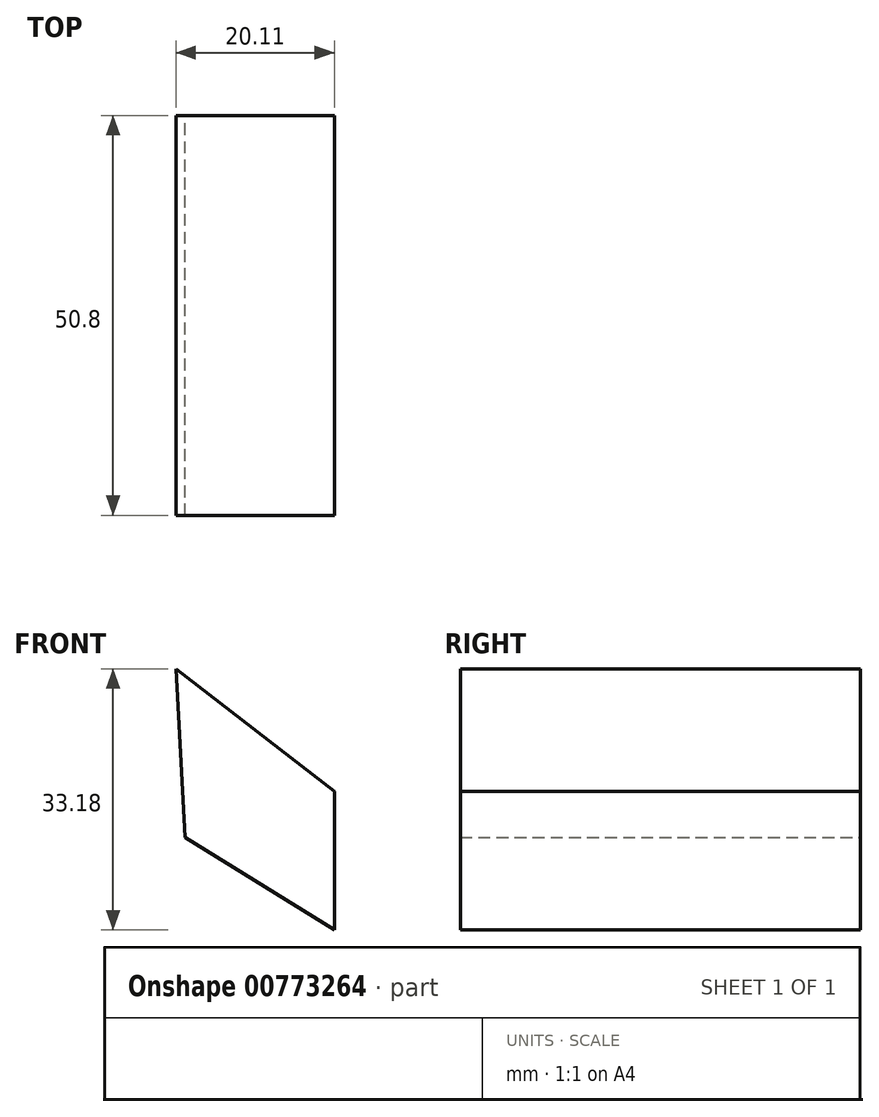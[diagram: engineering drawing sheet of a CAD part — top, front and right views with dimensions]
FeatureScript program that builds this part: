
annotation { "Feature Type Name" : "Feature", "Feature Type Description" : "" }
export const myFeature = defineFeature(function(context is Context, id is Id, definition is map)
    precondition{}
    {
        {
            var Q0;
            Q0=qCreatedBy(makeId("Front.planeOp"),FACE);
            var sketch = newSketch(context, id + "F0", { "sketchPlane" : qUnion([Q0])});
            skLineSegment(sketch, "E0", {"start": v(-20.11, 41.7) * mm, "end": v(0, 26.13) * mm});
            skLineSegment(sketch, "E1", {"start": v(0, 26.13) * mm, "end": v(0, 8.51) * mm});
            skLineSegment(sketch, "E2", {"start": v(0, 8.51) * mm, "end": v(-18.94, 20.26) * mm});
            skLineSegment(sketch, "E3", {"start": v(-18.94, 20.26) * mm, "end": v(-20.11, 41.7) * mm});
            skSolve(sketch);
        }
        {
            var Q0;
            Q0 = qSketchRegion(id + "F0", true);
            extrude(context, id + "F1", {"entities" : qUnion([Q0]), "depth" : 25.4 * mm, "offsetDistance" : 25.4 * mm});
        }
        {
            var Q0;
            Q0=makeQuery(id+"F1.opExtrude","SWEPT_BODY",BODY,{"disambiguationData":[OSD([sQuery(id+"F0.wireOp",EDGE,"E0"),sQuery(id+"F0.wireOp",EDGE,"E1"),sQuery(id+"F0.wireOp",EDGE,"E2"),sQuery(id+"F0.wireOp",EDGE,"E3")])]});
            var Q1;
            Q1=qCreatedBy(makeId("Front.planeOp"),FACE);
            mirror(context, id + "F2", {"operationType" : NewBodyOperationType.ADD, "entities" : qUnion([Q0]), "mirrorPlane" : qUnion([Q1])});
        }
    });
